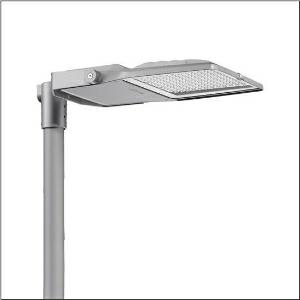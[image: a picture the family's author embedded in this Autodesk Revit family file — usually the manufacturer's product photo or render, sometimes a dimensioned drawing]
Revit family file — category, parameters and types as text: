
# Revit family: floodlight_fl_21_midi___pl52_5xa7782f2d3a_612a
name_source: partatom
category: Lighting Fixtures
units: mm (PartAtom-declared; Revit-internal decimal feet)

## family parameters
Cut with Voids When Loaded = No
Host = Face
Light Source = No
Part Type = Normal
Room Calculation Point = No
Round Connector Dimension = Use Diameter
Shared = No

## types (1)
- --- (1 x LED, 35760 lm, 270.2 W, 3000K)
    Apparent Load = 270 VA
    CIE Flux Codes = 26 60 98 100 100
    Color Rendering = 70
    Color Temperature = 3000K
    Default Elevation = 1800 mm
    Description = Floodlight FL 21 midi, floodlight, primary light control with lens, of PMMA, primary optical cover: protective disc, of toughened safety glass, transparent, light distribution: PL52, light emission: direct distribution, installation type: surface-mounted, LED, High Power LED, rated luminous flux: 35.760lm, luminous efficacy: 132lm/W, light colour: 730, colour temperature: 3000K, control gear: ECG iQ, control: optimised constant luminous flux control (CLO 2.0), Desk-Remote (wireless, voltage-free reading and setting of iQ features in the workshop via application-optimized NFC function/RFID function), Smart-Wire, Night-Set, Temp-Guard, Auto-Match, Street-Remote, with terminal, 6-pole, mains connection: 220..240V, AC, 50/60Hz, start of lifetime: 270W, end of lifetime: 286W, reduction: 132W, luminaire housing, of diecast aluminium, powder-coated, Siteco® metallic grey (DB 702S), corrosivity category C5 according to DIN EN ISO 12944, mast bracket, of steel, galvanised, powder-coated, Siteco® metallic grey (DB 702S), protection rating (complete): IP66, insulation class (complete): insulation class II (safety insulation), certification: CE, protection symbol: D, impact resistance: IK08, permissible operating ambient temperature: -40..+40°C, permissible operating ambient temperature for outdoor applications: -40..+50°C, standard: DIN EN 12944, packaging unit: 1 piece

Light Distribution: PL52
    Height = 76 mm
    Lamp = 1 x LED
    Lamp Light Flux = 35760 lm
    Lamp Power = 270.2 W
    Lamp count = 1
    Length = 657 mm
    Luminous efficacy = 132 lm/W
    Manufacturer = Siteco
    ModVariant = No
    Model = 5XA7782F2D3A
    Number of Poles = 1
    OnlyDefault = Yes
    Power Factor = 1
    Product Name = Floodlight FL 21 midi | PL52
    Product group = floodlight | pylon top
    ProductGroupID = 6101
    Protection Class = Protection class II
    Protection Degree = IP 66
    RLX_Detail_Level = 1
    RlxData = <blob elided: 153505 chars, md5=3b88493f>
    Socket = socket
    Standby Power = 0 W
    System Light Flux = 35760 lm
    System Power = 270 W
    Type Comments = factory setting: luminous flux: 100 % | dim-lin: 254 | 620 mA
    Type Image = l_1007123.jpg
    URL = http://relux.com
    VarID = @adj_014241
    Voltage = 0 V
    Weight = 0.00 kg
    Width = 442 mm

## geometry (parser evidence)
native form markers: Blend x4, Sweep x13
no freeform markers — native parametric forms only
